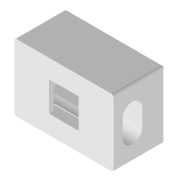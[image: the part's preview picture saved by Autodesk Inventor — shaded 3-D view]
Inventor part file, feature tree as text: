
AUTODESK INVENTOR PART (.ipt)
format: ipt  version: 2022 (Build 260153000, 153)  size: 929,792 bytes
history: native  units: mm
features: extrude x6, other x6, sketch x6, reference x4, projected_geometry x4, imported_body x1, plane x1, chamfer x1
ambient origin geometry x8: Origin, YZ Plane, XZ Plane, XY Plane, X Axis, Y Axis, Z Axis, Center Point
bodies: Volumenkörper4 (feature_tree)
feature tree (29):
  extrude  "Extrusion2"  Depth=11.0mm TaperAngle=0.0deg
  imported_body  "Basis2"
  other  "Kombinieren1"
  extrude  "Extrusion4"  Depth=10.0mm TaperAngle=0.0deg
  extrude  "Extrusion5"  Depth=7.9mm
  plane  "Arbeitsebene2"
  extrude  "Extrusion6"  Depth=12.0mm TaperAngle=0.0deg
  extrude  "Extrusion7"  Depth=1.0mm
  extrude  "Extrusion8"  Depth=10.0mm TaperAngle=0.0deg
  chamfer  "Fase1"  Distance=1.0mm Angle=45.0deg
  sketch  "Skizze1"  dims[d2=10.0mm d3=0.0mm d7=11.0mm d8=0.0mm]
  reference  "Referenz1"
  sketch  "Skizze3"  dims[d9=0.4mm d10=10.0mm d11=0.0mm]
  projected_geometry  "Projizierte Kontur1"
  sketch  "Skizze4"  dims[d12=0.5mm d13=7.9mm]
  projected_geometry  "Projizierte Kontur2"
  reference  "Referenz3"
  reference  "Referenz4"
  sketch  "Skizze5"  dims[d14=8.0mm d15=12.0mm d16=0.0mm]
  projected_geometry  "Projizierte Kontur3"
  sketch  "Skizze6"  dims[d17=12.0mm d18=0.0mm d19=1.0mm]
  projected_geometry  "Projizierte Kontur4"
  sketch  "Skizze7"  dims[d20=45.0deg d21=10.0mm d22=0.0mm d23=1.0mm d24=2.0mm d25=45.0deg]
  reference  "Referenz5"
  other  "Baugruppe5"
  other  "00_ESP3-CAM:1"
  other  "Bauteil50"
  other  "IM_Matchboxscope_base:1"
  other  "00_Seeeduino Xiao:2"
